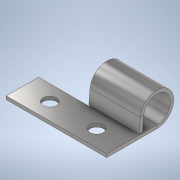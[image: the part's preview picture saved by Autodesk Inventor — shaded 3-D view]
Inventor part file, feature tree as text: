
AUTODESK INVENTOR PART (.ipt)
format: ipt  version: 2022 (Build 260153000, 153)  size: 161,280 bytes
history: native  units: mm
features: other x8, sketch x5, hole x1
ambient origin geometry x8: Origin, YZ Plane, XZ Plane, XY Plane, X Axis, Y Axis, Z Axis, Center Point
bodies: Body1 (feature_tree)
feature tree (14):
  other  "Sólido1"
  other  "Flange de contorno1"
  other  "Borda1"
  hole  "Furo1"  [1 undecoded]
  sketch  "Esboço1"  dims[d0=15.0mm d1=0.5mm]
  other  "Placa1"
  other  "Vergadura1"
  other  "Canto1"
  sketch  "Esboço2"  dims[d2=0.5mm]
  sketch  "Esboço4"  dims[d4=1.0mm]
  sketch  "Esboço5"  dims[d5=0.5mm d6=10.0mm d7=0.5mm d8=0.5mm d9=2.0mm d10=0.5mm d11=0.5mm d12=5.0mm d13=0.5mm d14=0.0mm d15=0.5mm d16=0.25mm d17=1.0mm d18=0.5mm d19=46.251225mm d20=2.0mm d21=2.0mm d22=2.0mm d23=6.0mm d24=4.0mm d25=2.0mm d26=90.0deg d27=0.5mm d28=20.594885mm d29=0.5mm d30=0.0mm]
  other  "Recortar1"
  other  "Recortar2"
  sketch  "Esboço3"  dims[d3=0.25mm]
note: 1 required parameter value undecoded (feature->parameter linkage not recoverable at this tier; creation-order binding heuristic only, values carry confidence <= 0.55)
